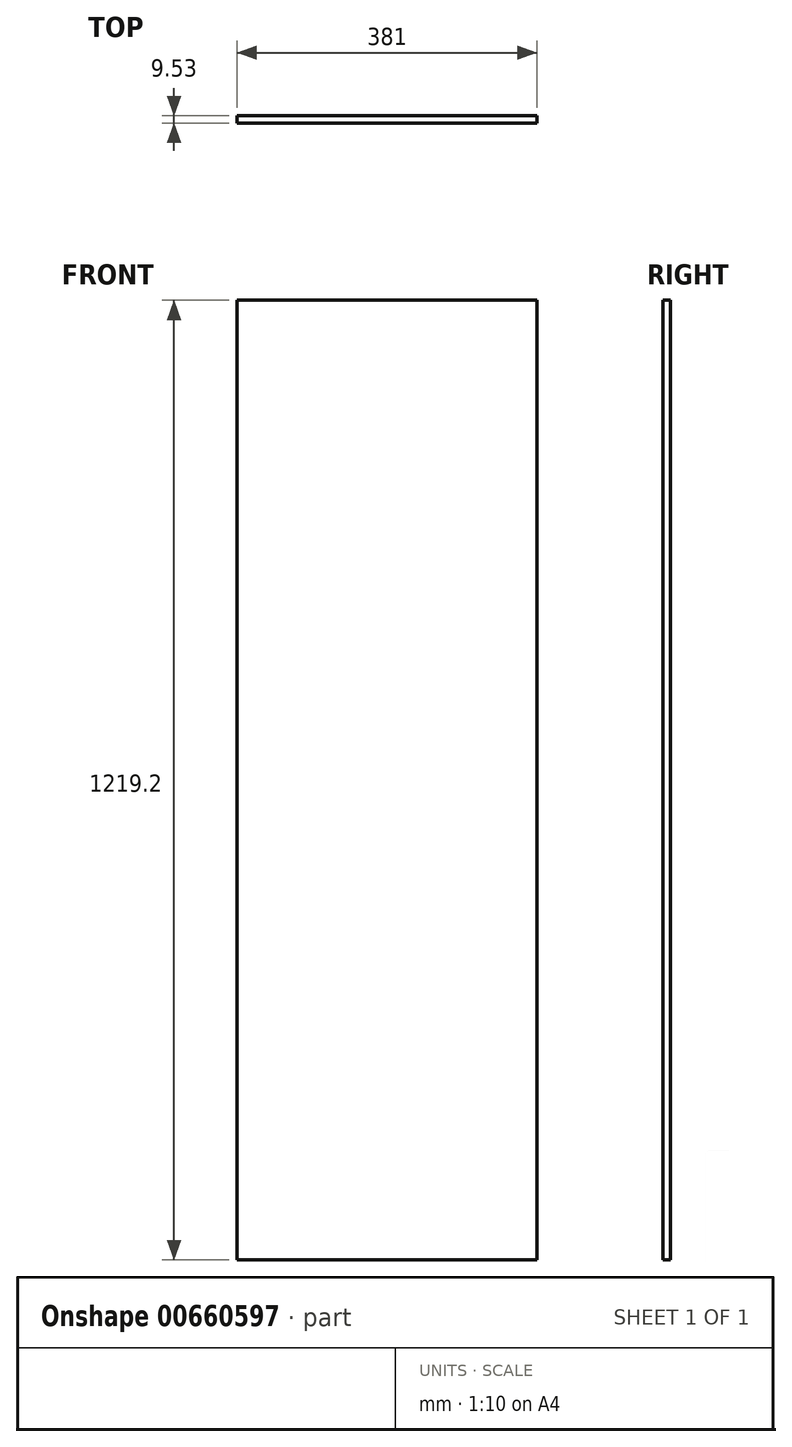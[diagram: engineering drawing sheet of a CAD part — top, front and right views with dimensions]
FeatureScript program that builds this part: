
annotation { "Feature Type Name" : "Feature", "Feature Type Description" : "" }
export const myFeature = defineFeature(function(context is Context, id is Id, definition is map)
    precondition{}
    {
        {
            var Q0;
            Q0=qCreatedBy(makeId("Front.planeOp"),FACE);
            var sketch = newSketch(context, id + "F0", { "sketchPlane" : qUnion([Q0])});
            skLineSegment(sketch, "E0.bottom", {"start": v(190.5, 609.6) * mm, "end": v(-190.5, 609.6) * mm});
            skLineSegment(sketch, "E0.top", {"start": v(190.5, -609.6) * mm, "end": v(-190.5, -609.6) * mm});
            skLineSegment(sketch, "E0.left", {"start": v(190.5, 609.6) * mm, "end": v(190.5, -609.6) * mm});
            skLineSegment(sketch, "E0.right", {"start": v(-190.5, 609.6) * mm, "end": v(-190.5, -609.6) * mm});
            skPoint(sketch, "E0.middle", {"position": v(0, 0) * mm});
            skSolve(sketch);
        }
        {
            var Q0;
            Q0 = qSketchRegion(id + "F0", true);
            extrude(context, id + "F1", {"entities" : qUnion([Q0]), "oppositeDirection" : true, "depth" : 9.52 * mm, "offsetDistance" : 25.4 * mm});
        }
    });
